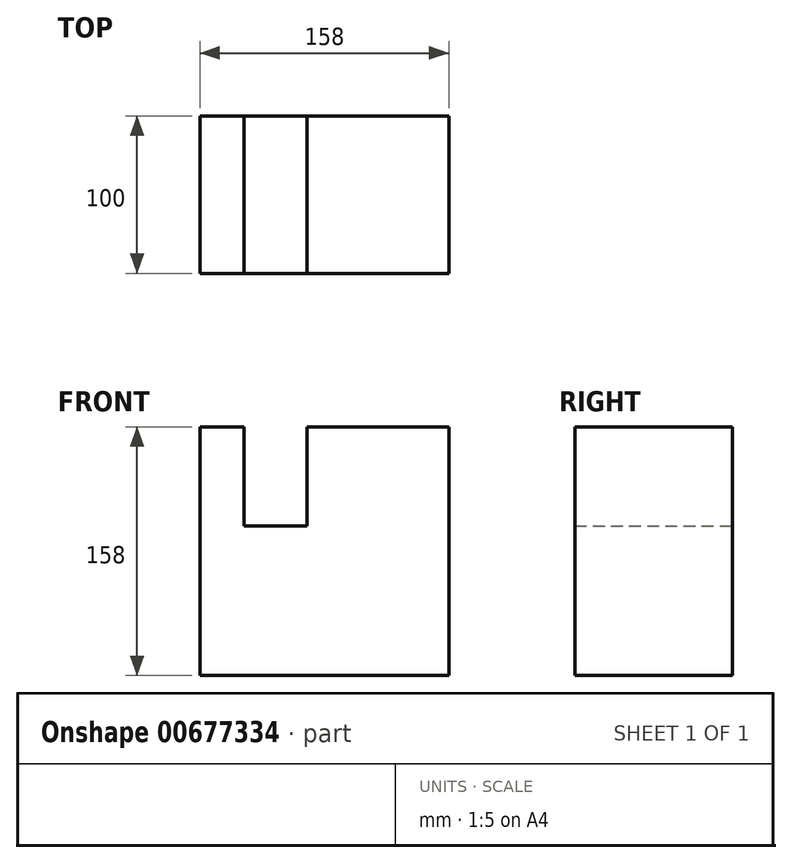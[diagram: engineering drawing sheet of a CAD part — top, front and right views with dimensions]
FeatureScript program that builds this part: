
annotation { "Feature Type Name" : "Feature", "Feature Type Description" : "" }
export const myFeature = defineFeature(function(context is Context, id is Id, definition is map)
    precondition{}
    {
        {
            var Q0;
            Q0=qCreatedBy(makeId("Front.planeOp"),FACE);
            var sketch = newSketch(context, id + "F0", { "sketchPlane" : qUnion([Q0])});
            skLineSegment(sketch, "E0", {"start": v(-80.85, 0) * mm, "end": v(77.15, 0) * mm});
            skLineSegment(sketch, "E1", {"start": v(77.15, 0) * mm, "end": v(77.15, 158) * mm});
            skLineSegment(sketch, "E2", {"start": v(77.15, 158) * mm, "end": v(-12.85, 158) * mm});
            skLineSegment(sketch, "E3", {"start": v(-12.85, 158) * mm, "end": v(-12.85, 95) * mm});
            skLineSegment(sketch, "E4", {"start": v(-12.85, 95) * mm, "end": v(-52.85, 95) * mm});
            skLineSegment(sketch, "E5", {"start": v(-52.85, 95) * mm, "end": v(-52.85, 158) * mm});
            skLineSegment(sketch, "E6", {"start": v(-52.85, 158) * mm, "end": v(-80.85, 158) * mm});
            skLineSegment(sketch, "E7", {"start": v(-80.85, 158) * mm, "end": v(-80.85, 0) * mm});
            skSolve(sketch);
        }
        {
            var Q0;
            Q0=qSketchRegion(id+"F0",true);
            extrude(context, id + "F1", {"entities" : qUnion([Q0]), "depth" : 100 * mm, "offsetDistance" : 25 * mm});
        }
    });
